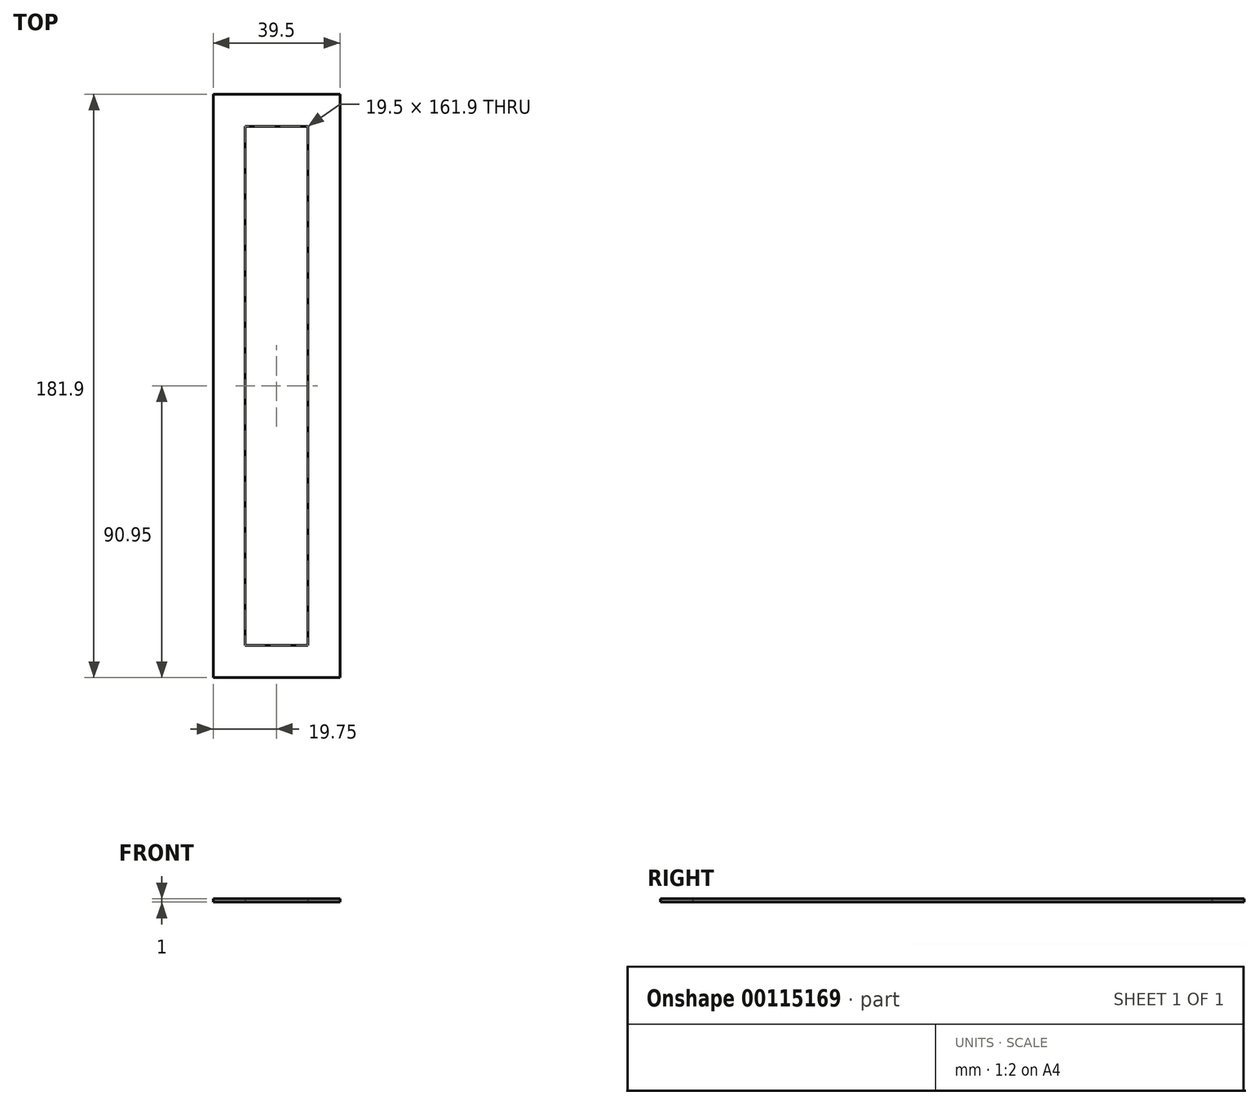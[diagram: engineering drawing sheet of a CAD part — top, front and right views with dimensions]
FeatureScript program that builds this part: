
annotation { "Feature Type Name" : "Feature", "Feature Type Description" : "" }
export const myFeature = defineFeature(function(context is Context, id is Id, definition is map)
    precondition{}
    {
        {
            var Q0;
            Q0=qCreatedBy(makeId("Top.planeOp"),FACE);
            var sketch = newSketch(context, id + "F0", { "sketchPlane" : qUnion([Q0])});
            skLineSegment(sketch, "E0.bottom", {"start": v(9.75, -80.95) * mm, "end": v(-9.75, -80.95) * mm});
            skLineSegment(sketch, "E0.top", {"start": v(9.75, 80.95) * mm, "end": v(-9.75, 80.95) * mm});
            skLineSegment(sketch, "E0.left", {"start": v(9.75, -80.95) * mm, "end": v(9.75, 80.95) * mm});
            skLineSegment(sketch, "E0.right", {"start": v(-9.75, -80.95) * mm, "end": v(-9.75, 80.95) * mm});
            skPoint(sketch, "E0.middle", {"position": v(0, 0) * mm});
            skLineSegment(sketch, "E1.0", {"start": v(19.75, 90.95) * mm, "end": v(-19.75, 90.95) * mm});
            skLineSegment(sketch, "E1.1", {"start": v(19.75, -90.95) * mm, "end": v(19.75, 90.95) * mm});
            skLineSegment(sketch, "E1.2", {"start": v(19.75, -90.95) * mm, "end": v(-19.75, -90.95) * mm});
            skLineSegment(sketch, "E1.3", {"start": v(-19.75, -90.95) * mm, "end": v(-19.75, 90.95) * mm});
            skSolve(sketch);
        }
        {
            var Q0;
            Q0=makeQuery(id+"F0.imprint","IMPRINT",FACE,{"disambiguationData":[TD([[makeQuery(id+"F0.imprint","IMPRINT",EDGE,{"derivedFrom":sQuery(id+"F0.wireOp",EDGE,"E0.bottom")}),1.0]])]});
            extrude(context, id + "F1", {"entities" : qUnion([Q0]), "depth" : 1 * mm});
        }
    });
